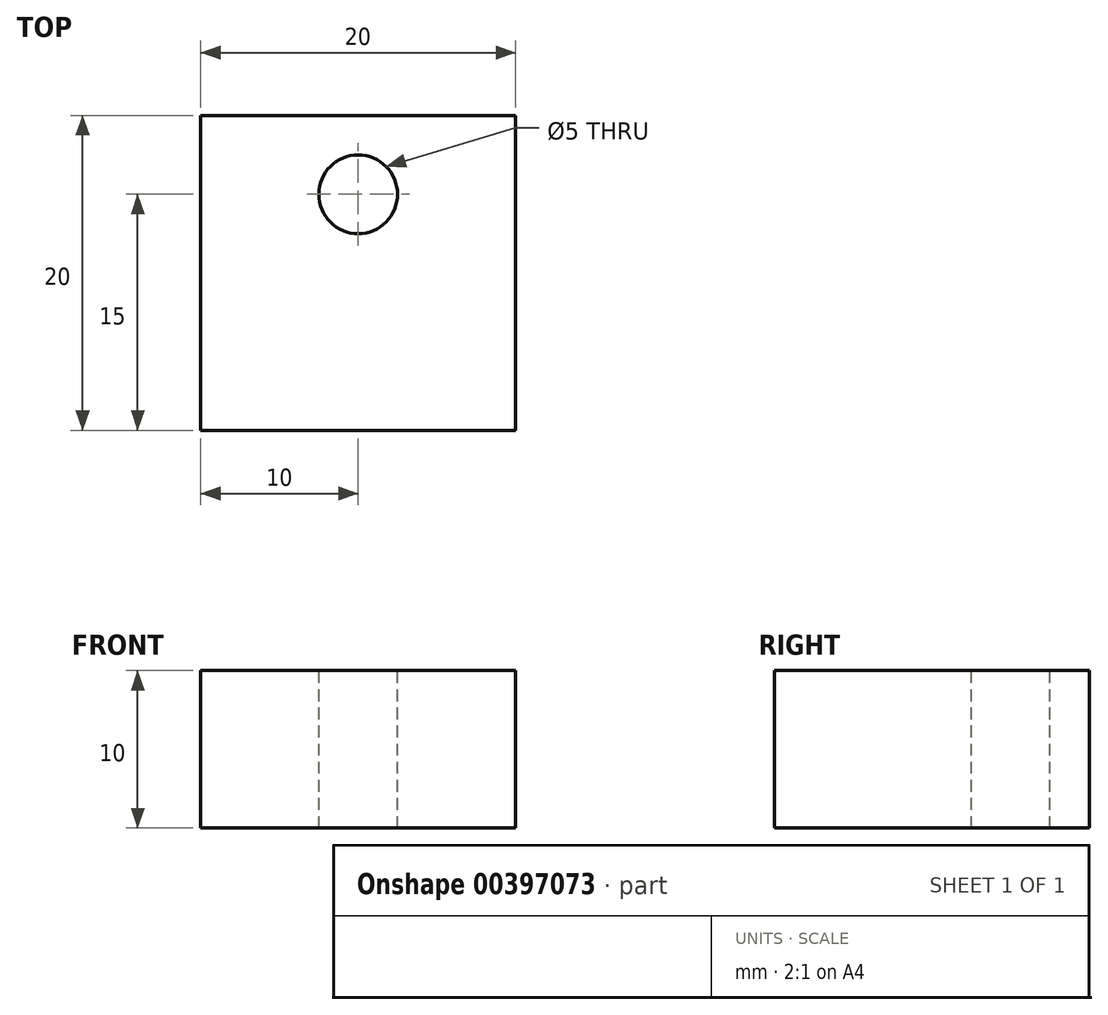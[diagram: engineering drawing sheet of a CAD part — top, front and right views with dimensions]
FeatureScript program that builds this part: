
annotation { "Feature Type Name" : "Feature", "Feature Type Description" : "" }
export const myFeature = defineFeature(function(context is Context, id is Id, definition is map)
    precondition{}
    {
        {
            var Q0;
            Q0=qCreatedBy(makeId("Top.planeOp"),FACE);
            var sketch = newSketch(context, id + "F0", { "sketchPlane" : qUnion([Q0])});
            skLineSegment(sketch, "E0.bottom", {"start": v(10, -10) * mm, "end": v(-10, -10) * mm});
            skLineSegment(sketch, "E0.top", {"start": v(10, 10) * mm, "end": v(-10, 10) * mm});
            skLineSegment(sketch, "E0.left", {"start": v(10, -10) * mm, "end": v(10, 10) * mm});
            skLineSegment(sketch, "E0.right", {"start": v(-10, -10) * mm, "end": v(-10, 10) * mm});
            skPoint(sketch, "E0.middle", {"position": v(0, 0) * mm});
            skSolve(sketch);
        }
        {
            var Q0;
            Q0=qSketchRegion(id+"F0",true);
            extrude(context, id + "F1", {"entities" : qUnion([Q0]), "depth" : 10 * mm});
        }
        {
            var Q0;
            Q0=makeQuery(id+"F1.opExtrude","CAP_FACE",FACE,{"disambiguationData":[OSD([sQuery(id+"F0.wireOp",EDGE,"E0.bottom"),sQuery(id+"F0.wireOp",EDGE,"E0.top"),sQuery(id+"F0.wireOp",EDGE,"E0.left"),sQuery(id+"F0.wireOp",EDGE,"E0.right")])],"isStart":false});
            var sketch = newSketch(context, id + "F2", { "sketchPlane" : qUnion([Q0])});
            skPoint(sketch, "E1", {"position": v(0, 5) * mm});
            skPoint(sketch, "E1.positionSnap0", {"position": v(0, 10) * mm});
            skSolve(sketch);
        }
        {
            var Q0;
            Q0=sQuery(id+"F2.wireOp",VERTEX,"E1");
            var Q1;
            Q1=makeQuery(id+"F1.opExtrude","SWEPT_BODY",BODY,{"disambiguationData":[OSD([sQuery(id+"F0.wireOp",EDGE,"E0.bottom"),sQuery(id+"F0.wireOp",EDGE,"E0.top"),sQuery(id+"F0.wireOp",EDGE,"E0.left"),sQuery(id+"F0.wireOp",EDGE,"E0.right")])]});
            hole(context, id + "F3", {"style" : HoleStyle.SIMPLE, "endStyle" : HoleEndStyle.BLIND, "standardTappedOrClearance" : lookupTablePath({ "standard" : "ISO", "engagement" : "75%", "pitch" : "1 mm", "size" : "M6", "type" : "Tapped" }), "standardBlindInLast" : lookupTablePath({ "standard" : "ISO", "engagement" : "75%", "pitch" : "1 mm", "size" : "M6", "type" : "Tapped" }), "holeDiameter" : 5 * mm, "holeDepth" : 10 * mm, "locations" : qUnion([Q0]), "scope" : qUnion([Q1]), "majorDiameter" : 6 * mm});
        }
    });
